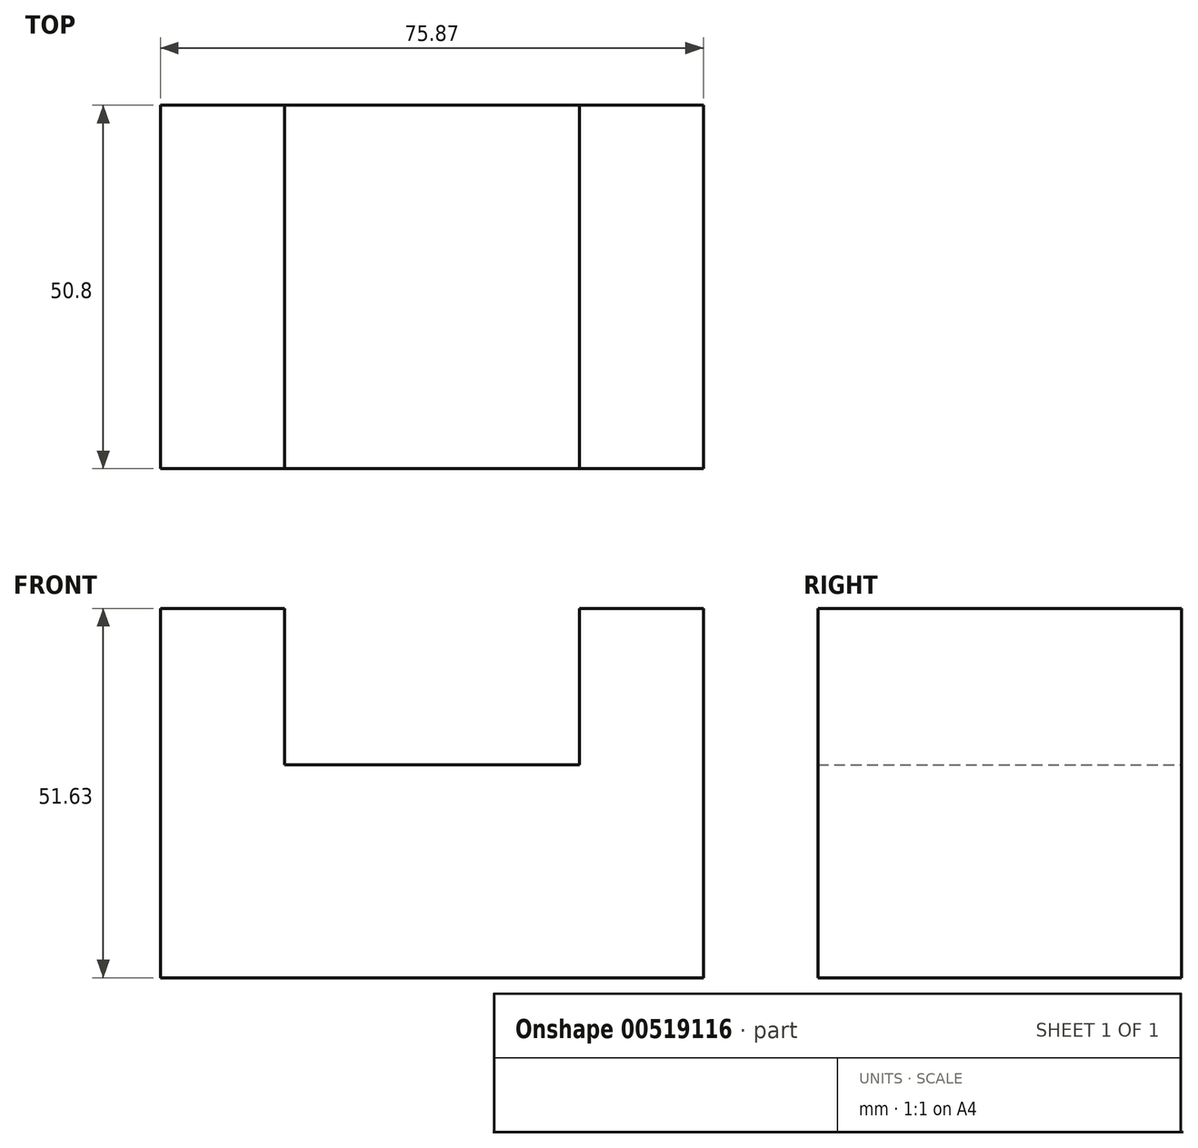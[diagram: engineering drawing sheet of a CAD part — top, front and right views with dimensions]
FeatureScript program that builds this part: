
annotation { "Feature Type Name" : "Feature", "Feature Type Description" : "" }
export const myFeature = defineFeature(function(context is Context, id is Id, definition is map)
    precondition{}
    {
        {
            var Q0;
            Q0=qCreatedBy(makeId("Front.planeOp"),FACE);
            var sketch = newSketch(context, id + "F0", { "sketchPlane" : qUnion([Q0])});
            skLineSegment(sketch, "E0.bottom", {"start": v(0, 0) * mm, "end": v(75.87, 0) * mm});
            skLineSegment(sketch, "E0.top", {"start": v(0, 51.63) * mm, "end": v(17.34, 51.63) * mm});
            skLineSegment(sketch, "E0.left", {"start": v(0, 0) * mm, "end": v(0, 51.63) * mm});
            skLineSegment(sketch, "E0.right", {"start": v(75.87, 0) * mm, "end": v(75.87, 51.63) * mm});
            skLineSegment(sketch, "E1.top", {"start": v(17.34, 29.76) * mm, "end": v(58.53, 29.76) * mm});
            skLineSegment(sketch, "E1.left", {"start": v(17.34, 51.63) * mm, "end": v(17.34, 29.76) * mm});
            skLineSegment(sketch, "E1.right", {"start": v(58.53, 51.63) * mm, "end": v(58.53, 29.76) * mm});
            skLineSegment(sketch, "E2.trimOffspring", {"start": v(58.53, 51.63) * mm, "end": v(75.87, 51.63) * mm});
            skSolve(sketch);
        }
        {
            var Q0;
            Q0=makeQuery(id+"F0.imprint","IMPRINT",FACE,{"disambiguationData":[TD([[makeQuery(id+"F0.imprint","IMPRINT",EDGE,{"derivedFrom":sQuery(id+"F0.wireOp",EDGE,"E0.bottom")}),1.0]])]});
            extrude(context, id + "F1", {"entities" : qUnion([Q0]), "depth" : 50.8 * mm});
        }
    });
